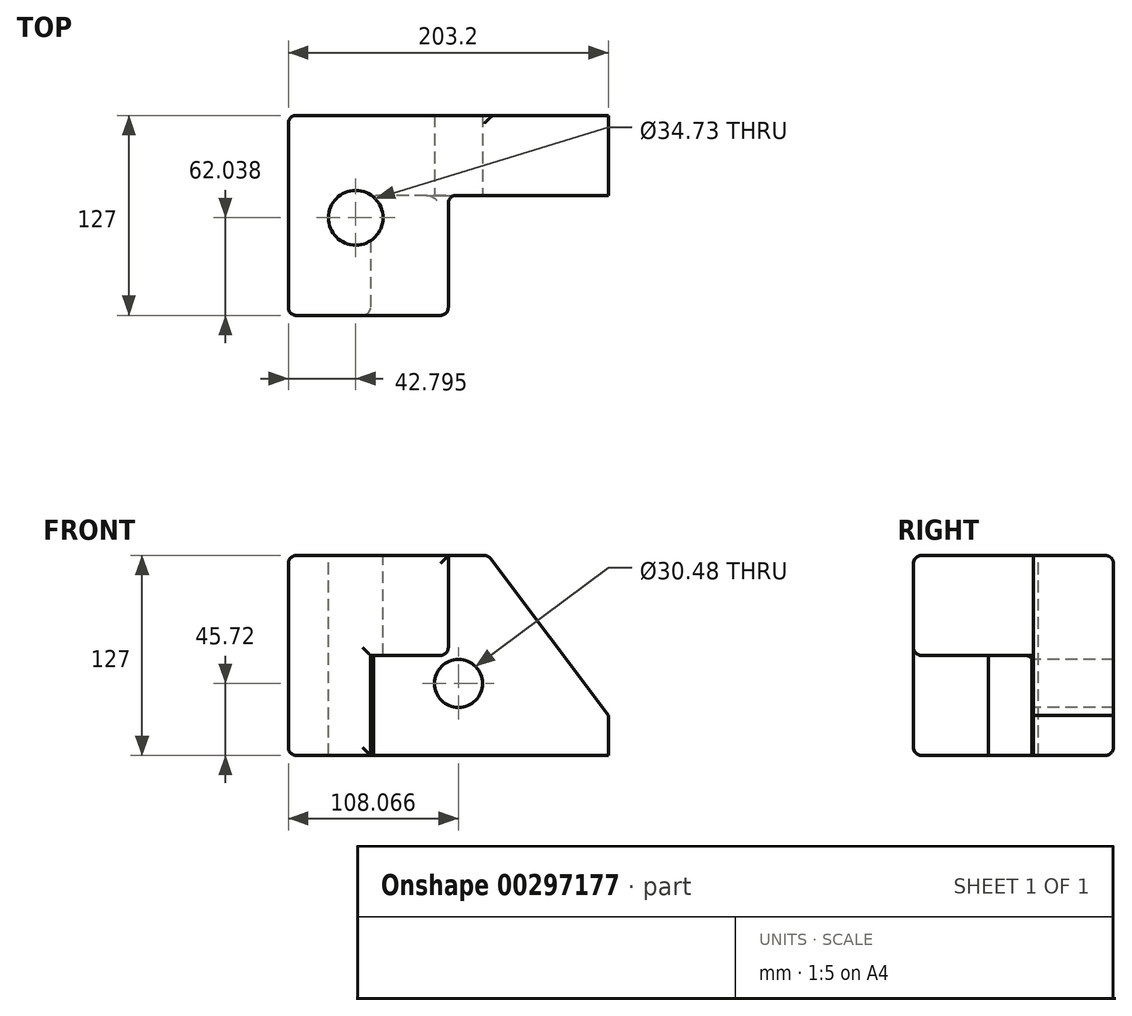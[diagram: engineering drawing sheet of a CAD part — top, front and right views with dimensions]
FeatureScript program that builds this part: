
annotation { "Feature Type Name" : "Feature", "Feature Type Description" : "" }
export const myFeature = defineFeature(function(context is Context, id is Id, definition is map)
    precondition{}
    {
        {
            var Q0;
            Q0=qCreatedBy(makeId("Front.planeOp"),FACE);
            var sketch = newSketch(context, id + "F0", { "sketchPlane" : qUnion([Q0])});
            skLineSegment(sketch, "E0.bottom", {"start": v(101.6, -63.5) * mm, "end": v(-101.6, -63.5) * mm});
            skLineSegment(sketch, "E0.top", {"start": v(101.6, 63.5) * mm, "end": v(-101.6, 63.5) * mm});
            skLineSegment(sketch, "E0.left", {"start": v(101.6, -63.5) * mm, "end": v(101.6, 63.5) * mm});
            skLineSegment(sketch, "E0.right", {"start": v(-101.6, -63.5) * mm, "end": v(-101.6, 63.5) * mm});
            skPoint(sketch, "E0.middle", {"position": v(0, 0) * mm});
            skSolve(sketch);
        }
        {
            var Q0;
            Q0=makeQuery(id+"F0.imprint","IMPRINT",FACE,{"disambiguationData":[TD([[makeQuery(id+"F0.imprint","IMPRINT",EDGE,{"derivedFrom":sQuery(id+"F0.wireOp",EDGE,"E0.bottom")}),-1.0]])]});
            extrude(context, id + "F1", {"entities" : qUnion([Q0]), "depth" : 127 * mm});
        }
        {
            var Q0;
            Q0=makeQuery(id+"F1.opExtrude","CAP_FACE",FACE,{"disambiguationData":[OSD([sQuery(id+"F0.wireOp",EDGE,"E0.bottom"),sQuery(id+"F0.wireOp",EDGE,"E0.top"),sQuery(id+"F0.wireOp",EDGE,"E0.left"),sQuery(id+"F0.wireOp",EDGE,"E0.right")])],"isStart":false});
            var sketch = newSketch(context, id + "F2", { "sketchPlane" : qUnion([Q0])});
            skLineSegment(sketch, "E1", {"start": v(0, 63.5) * mm, "end": v(0, 0) * mm});
            skLineSegment(sketch, "E2", {"start": v(0, 0) * mm, "end": v(-49.41, 0) * mm});
            skPoint(sketch, "E2.endSnap0", {"position": v(-101.6, 0) * mm});
            skLineSegment(sketch, "E3", {"start": v(-49.41, 0) * mm, "end": v(-49.41, -63.5) * mm});
            skLineSegment(sketch, "E4", {"start": v(-49.41, -63.5) * mm, "end": v(-101.6, -63.5) * mm});
            skLineSegment(sketch, "E5", {"start": v(-101.6, -63.5) * mm, "end": v(-101.6, 63.5) * mm});
            skLineSegment(sketch, "E6", {"start": v(-101.6, 63.5) * mm, "end": v(0, 63.5) * mm});
            skSolve(sketch);
        }
        {
            var Q0;
            {var subQ3=sQuery(id+"F2.wireOp",EDGE,"E1");Q0=makeQuery(id+"F2.imprint","IMPRINT",FACE,{"disambiguationData":[TD([[makeQuery(id+"F2.imprint","IMPRINT",EDGE,{"derivedFrom":subQ3}),1.0]])]});}
            extrude(context, id + "F3", {"entities" : qUnion([Q0]), "operationType" : NewBodyOperationType.REMOVE, "oppositeDirection" : true, "depth" : 76.2 * mm});
        }
        {
            var Q0;
            Q0=makeQuery(id+"F1.opExtrude","SWEPT_EDGE",EDGE,{"disambiguationData":[OSD([sQuery(id+"F0.wireOp",EDGE,"E0.top"),sQuery(id+"F0.wireOp",EDGE,"E0.left")])]});
            chamfer(context, id + "F4", {"entities" : qUnion([Q0]), "chamferType" : ChamferType.TWO_OFFSETS, "width1" : 76.2 * mm, "oppositeDirection" : false, "width2" : 101.6 * mm, "tangentPropagation" : true});
        }
        {
            var Q0;
            {var subQ0=sQuery(id+"F0.wireOp",EDGE,"E0.top");Q0=makeQuery(id+"F4.opChamfer","BLEND_EDGE",EDGE,{"blendedFrom":[makeQuery(id+"F1.opExtrude","SWEPT_EDGE",EDGE,{"disambiguationData":[OSD([subQ0,sQuery(id+"F0.wireOp",EDGE,"E0.left")])]}),makeQuery(id+"F1.opExtrude","SWEPT_FACE",FACE,{"disambiguationData":[OSD([subQ0])]})],"blendedInto":[makeQuery(id+"F1.opExtrude","SWEPT_FACE",FACE,{"disambiguationData":[OSD([subQ0])]})]});}
            var Q1;
            Q1=makeQuery(id+"F3.boolean.opBoolean","COPY",EDGE,{"derivedFrom":makeQuery(id+"F3.opExtrude","CAP_EDGE",EDGE,{"disambiguationData":[OSD([sQuery(id+"F0.wireOp",EDGE,"E0.top")])],"isStart":false})});
            var Q2;
            Q2=makeQuery(id+"F3.boolean.opBoolean","COPY",EDGE,{"derivedFrom":makeQuery(id+"F3.opExtrude","SWEPT_EDGE",EDGE,{"disambiguationData":[OSD([sQuery(id+"F0.wireOp",EDGE,"E0.top"),sQuery(id+"F2.wireOp",EDGE,"E1"),sQuery(id+"F2.wireOp",EDGE,"E6")])]})});
            var Q3;
            Q3=makeQuery(id+"F1.opExtrude","CAP_EDGE",EDGE,{"disambiguationData":[OSD([sQuery(id+"F0.wireOp",EDGE,"E0.top")])],"isStart":false});
            var Q4;
            Q4=makeQuery(id+"F1.opExtrude","SWEPT_EDGE",EDGE,{"disambiguationData":[OSD([sQuery(id+"F0.wireOp",EDGE,"E0.top"),sQuery(id+"F0.wireOp",EDGE,"E0.right")])]});
            var Q5;
            Q5=makeQuery(id+"F1.opExtrude","CAP_EDGE",EDGE,{"disambiguationData":[OSD([sQuery(id+"F0.wireOp",EDGE,"E0.top")])],"isStart":true});
            var Q6;
            Q6=makeQuery(id+"F1.opExtrude","CAP_EDGE",EDGE,{"disambiguationData":[OSD([sQuery(id+"F0.wireOp",EDGE,"E0.right")])],"isStart":false});
            var Q7;
            Q7=makeQuery(id+"F3.boolean.opBoolean","COPY",EDGE,{"derivedFrom":makeQuery(id+"F3.opExtrude","CAP_EDGE",EDGE,{"disambiguationData":[OSD([sQuery(id+"F2.wireOp",EDGE,"E3")])],"isStart":true})});
            var Q8;
            Q8=makeQuery(id+"F3.boolean.opBoolean","COPY",EDGE,{"derivedFrom":makeQuery(id+"F3.opExtrude","CAP_EDGE",EDGE,{"disambiguationData":[OSD([sQuery(id+"F2.wireOp",EDGE,"E2")])],"isStart":true})});
            var Q9;
            Q9=makeQuery(id+"F3.boolean.opBoolean","COPY",EDGE,{"derivedFrom":makeQuery(id+"F3.opExtrude","SWEPT_EDGE",EDGE,{"disambiguationData":[OSD([sQuery(id+"F2.wireOp",EDGE,"E1"),sQuery(id+"F2.wireOp",EDGE,"E2")])]})});
            var Q10;
            Q10=makeQuery(id+"F1.opExtrude","CAP_FACE",FACE,{"disambiguationData":[OSD([sQuery(id+"F0.wireOp",EDGE,"E0.bottom"),sQuery(id+"F0.wireOp",EDGE,"E0.top"),sQuery(id+"F0.wireOp",EDGE,"E0.left"),sQuery(id+"F0.wireOp",EDGE,"E0.right")])],"isStart":false});
            var Q11;
            Q11=makeQuery(id+"F3.boolean.opBoolean","COPY",EDGE,{"derivedFrom":makeQuery(id+"F3.opExtrude","CAP_EDGE",EDGE,{"disambiguationData":[OSD([sQuery(id+"F2.wireOp",EDGE,"E1")])],"isStart":false})});
            var Q12;
            Q12=makeQuery(id+"F1.opExtrude","CAP_EDGE",EDGE,{"disambiguationData":[OSD([sQuery(id+"F0.wireOp",EDGE,"E0.bottom")])],"isStart":false});
            var Q13;
            Q13=makeQuery(id+"F1.opExtrude","CAP_EDGE",EDGE,{"disambiguationData":[OSD([sQuery(id+"F0.wireOp",EDGE,"E0.right")])],"isStart":true});
            var Q14;
            Q14=makeQuery(id+"F1.opExtrude","SWEPT_EDGE",EDGE,{"disambiguationData":[OSD([sQuery(id+"F0.wireOp",EDGE,"E0.bottom"),sQuery(id+"F0.wireOp",EDGE,"E0.right")])]});
            var Q15;
            Q15=makeQuery(id+"F1.opExtrude","CAP_EDGE",EDGE,{"disambiguationData":[OSD([sQuery(id+"F0.wireOp",EDGE,"E0.bottom")])],"isStart":true});
            var Q16;
            Q16=makeQuery(id+"F3.boolean.opBoolean","COPY",EDGE,{"derivedFrom":makeQuery(id+"F3.opExtrude","CAP_EDGE",EDGE,{"disambiguationData":[OSD([sQuery(id+"F0.wireOp",EDGE,"E0.bottom")])],"isStart":false})});
            var Q17;
            Q17=makeQuery(id+"F3.boolean.opBoolean","COPY",EDGE,{"derivedFrom":makeQuery(id+"F3.opExtrude","SWEPT_EDGE",EDGE,{"disambiguationData":[OSD([sQuery(id+"F0.wireOp",EDGE,"E0.bottom"),sQuery(id+"F2.wireOp",EDGE,"E3"),sQuery(id+"F2.wireOp",EDGE,"E4")])]})});
            var Q18;
            Q18=makeQuery(id+"F3.boolean.opBoolean","COPY",EDGE,{"derivedFrom":makeQuery(id+"F3.opExtrude","CAP_EDGE",EDGE,{"disambiguationData":[OSD([sQuery(id+"F2.wireOp",EDGE,"E3")])],"isStart":false})});
            fillet(context, id + "F5", {"entities" : qUnion([Q0, Q1, Q2, Q3, Q4, Q5, Q6, Q7, Q8, Q9, Q10, Q11, Q12, Q13, Q14, Q15, Q16, Q17, Q18]), "radius" : 5.08 * mm, "tangentPropagation" : true, "allowEdgeOverflow" : false});
        }
        {
            var Q0;
            Q0=makeQuery(id+"F3.boolean.opBoolean","COPY",FACE,{"derivedFrom":makeQuery(id+"F3.opExtrude","CAP_FACE",FACE,{"disambiguationData":[OSD([sQuery(id+"F0.wireOp",EDGE,"E0.bottom"),sQuery(id+"F0.wireOp",EDGE,"E0.top"),sQuery(id+"F0.wireOp",EDGE,"E0.left"),sQuery(id+"F2.wireOp",EDGE,"E1"),sQuery(id+"F2.wireOp",EDGE,"E2"),sQuery(id+"F2.wireOp",EDGE,"E3")])],"isStart":false})});
            var sketch = newSketch(context, id + "F6", { "sketchPlane" : qUnion([Q0])});
            skCircle(sketch, "E7", {"center": v(6.47, -17.78) * mm, "radius": 15.24 * mm});
            skSolve(sketch);
        }
        {
            var Q0;
            Q0=makeQuery(id+"F6.imprint","IMPRINT",FACE,{"disambiguationData":[TD([[makeQuery(id+"F6.imprint","IMPRINT",EDGE,{"derivedFrom":sQuery(id+"F6.wireOp",EDGE,"E7")}),1.0]])]});
            var Q1;
            Q1=makeQuery(id+"F1.opExtrude","CAP_FACE",FACE,{"disambiguationData":[OSD([sQuery(id+"F0.wireOp",EDGE,"E0.bottom"),sQuery(id+"F0.wireOp",EDGE,"E0.top"),sQuery(id+"F0.wireOp",EDGE,"E0.left"),sQuery(id+"F0.wireOp",EDGE,"E0.right")])],"isStart":true});
            extrude(context, id + "F7", {"entities" : qUnion([Q0]), "operationType" : NewBodyOperationType.REMOVE, "endBound" : BoundingType.UP_TO_SURFACE, "oppositeDirection" : true, "endBoundEntityFace" : qUnion([Q1]), "depth" : 25.4 * mm});
        }
        {
            var Q0;
            Q0=makeQuery(id+"F1.opExtrude","SWEPT_FACE",FACE,{"disambiguationData":[OSD([sQuery(id+"F0.wireOp",EDGE,"E0.top")])]});
            var sketch = newSketch(context, id + "F8", { "sketchPlane" : qUnion([Q0])});
            skCircle(sketch, "E8", {"center": v(-58.8, -64.96) * mm, "radius": 17.36 * mm});
            skSolve(sketch);
        }
        {
            var Q0;
            Q0=makeQuery(id+"F8.imprint","IMPRINT",FACE,{"disambiguationData":[TD([[makeQuery(id+"F8.imprint","IMPRINT",EDGE,{"derivedFrom":sQuery(id+"F8.wireOp",EDGE,"E8")}),1.0]])]});
            var Q1;
            Q1=makeQuery(id+"F1.opExtrude","SWEPT_FACE",FACE,{"disambiguationData":[OSD([sQuery(id+"F0.wireOp",EDGE,"E0.bottom")])]});
            extrude(context, id + "F9", {"entities" : qUnion([Q0]), "operationType" : NewBodyOperationType.REMOVE, "endBound" : BoundingType.UP_TO_SURFACE, "oppositeDirection" : true, "endBoundEntityFace" : qUnion([Q1]), "depth" : 25.4 * mm});
        }
    });
